# Revit family: REFLECT LED
name_source: partatom
category: Осветительные приборы
revit_build: Autodesk Revit 2016 (Build: 20150220_1215(x64)
units: mm (PartAtom-declared; Revit-internal decimal feet)

## family parameters
Источник света = Да
Общий = Нет
Основа = Грань
При загрузке вырезать с полостями = Нет
Размер круглого соединителя = Использовать диаметр
Тип детали = Нормальный
Точка расчета площади = Нет

## types (1)
- REFLECT LED
    ADSK_Единица измерения = Шт.
    ADSK_Завод-изготовитель = ООО МГК Световые технологии
    ADSK_Количество фаз = 1
    ADSK_Количество фаз числовое = 1
    ADSK_Коэффициент мощности = 0.92
    ADSK_Масса = 0
    ADSK_Наименование = Светодиодная подвесная модульная система для освещения офисных помещений класса А, кабинетов VIP-персон, шоу румов. В светильнике сочетаются дизайнерская внешность, высокая эффективность (>100 лм) и сверхкомфортный отраженный свет. Светильник REFLECT LED - когда свет и пространство на одной волне
    ADSK_Напряжение = 230 В
    ADSK_Номинальная мощность = 0 кВт
    ADSK_Полная мощность = 0 кВ·А
    ADSK_Размер_Длина = 224 мм
    ADSK_Размер_Ширина = 224 мм
    ADSK_Ток = 0 А
    ADSK_Энергоэффективность = 0 лм/Вт
    CL = Да
    CL.переходник = Да
    CL.подвес = Да
    CS = Да
    CS.переходник = Да
    CS.подвес = Да
    IP Class = IP20
    URL = http://ltcompany.com
    Блок аварийного питания = Нет
    Видимая форма излучения при визуализации = Нет
    Группа модели = Светильники
    Длина.отражатель = 800 мм
    Длина.свет = 724 мм
    Изготовитель = ООО МГК Световые технологии
    Излучение по длине прямоугольника = 224 мм
    Излучение по ширине прямоугольника = 800 мм
    Класс Защиты = I
    Класс пожароопасности = П-II,IIа
    Климатическая зона = УХЛ4
    Код по классификатору = D5020200
    Корпус = Металлик металл
    Область использования = HoReCa / гостиницы / рестораны / кафе Гипер- / супермаркеты Магазины / бутики Образовательные учреждения Офисно-административные объекты
    Описание = Светодиодная подвесная модульная система для освещения офисных помещений класса А, кабинетов VIP-персон, шоу румов. В светильнике сочетаются дизайнерская внешность, высокая эффективность (>100 лм) и сверхкомфортный отраженный свет. Светильник REFLECT LED - когда свет и пространство на одной волне
    Отметка по умолчанию = 0 мм
    Полная установленная мощность = 0 кВ·А
    Разработчик = ООО ПРОРУБИМ
    Разработчик (телефон) = +7 (495) 649-85-43
    Светофильтр = 16777215
    Смещение цветовой температуры при затухании лампы = <Нет>
    Тип ИС = LED
    Тип продукции = Светильники
    Угол наклона = -90.00°
    Файл фотометрической сетки = generic
    Шаг. подвесы = 575 мм
